# Revit family: Drain_Area_Planting-Zurn-Z349
name_source: partatom
category: Plumbing Fixtures
units: mm (PartAtom-declared; Revit-internal decimal feet)

## family parameters
Always vertical = Yes
Cut with Voids When Loaded = No
Maintain Annotation Orientation = No
OmniClass Number = 23.45.55.21
OmniClass Title = Drains (Wastes)
Part Type = Normal
Room Calculation Point = No
Round Connector Dimension = Use Radius
Shared = No
Work Plane-Based = No

## types (1)
- Load Family Type Catalog
    Approx. Weight (Lbs) = 40 "
    Assembly Code = D2040300
    Body Height_E = 5.25 "
    CW Connection = No
    CWFU = 0
    Clamp = Iron - Zurn - Cast - Painted - Blue
    Connector Radius = 1 "
    Default Elevation = 20 "
    Description = Terrace Planting Area Drain
    HW Connection = No
    HWFU = 0
    Main Material = Iron - Zurn - Cast - Painted - Blue
    Manufacturer = Zurn Water, LLC
    Manufacurer Brand = Zurn
    Model = Z349
    Modified Date = 02/13/2026
    Pipe Size_Inside Diameter = 2.067 "
    Pipe Size_Nominal Diameter = 2 "
    Pipe Size_Outer Diameter = 2.375 "
    Product Documentation Link = https://files.zurn.com
    Product Page URL = https://www.zurn.com
    Product data url = https://www.bimobject.com
    Type Comments = Z349-2 Inch-No-Hub Outlet
    URL = www.zurn.com
    Vent Connection = No
    WFU = 1
    Waste Connection = Yes

## geometry (parser evidence)
native form markers: Blend x6, Sweep x2
no freeform markers — native parametric forms only
